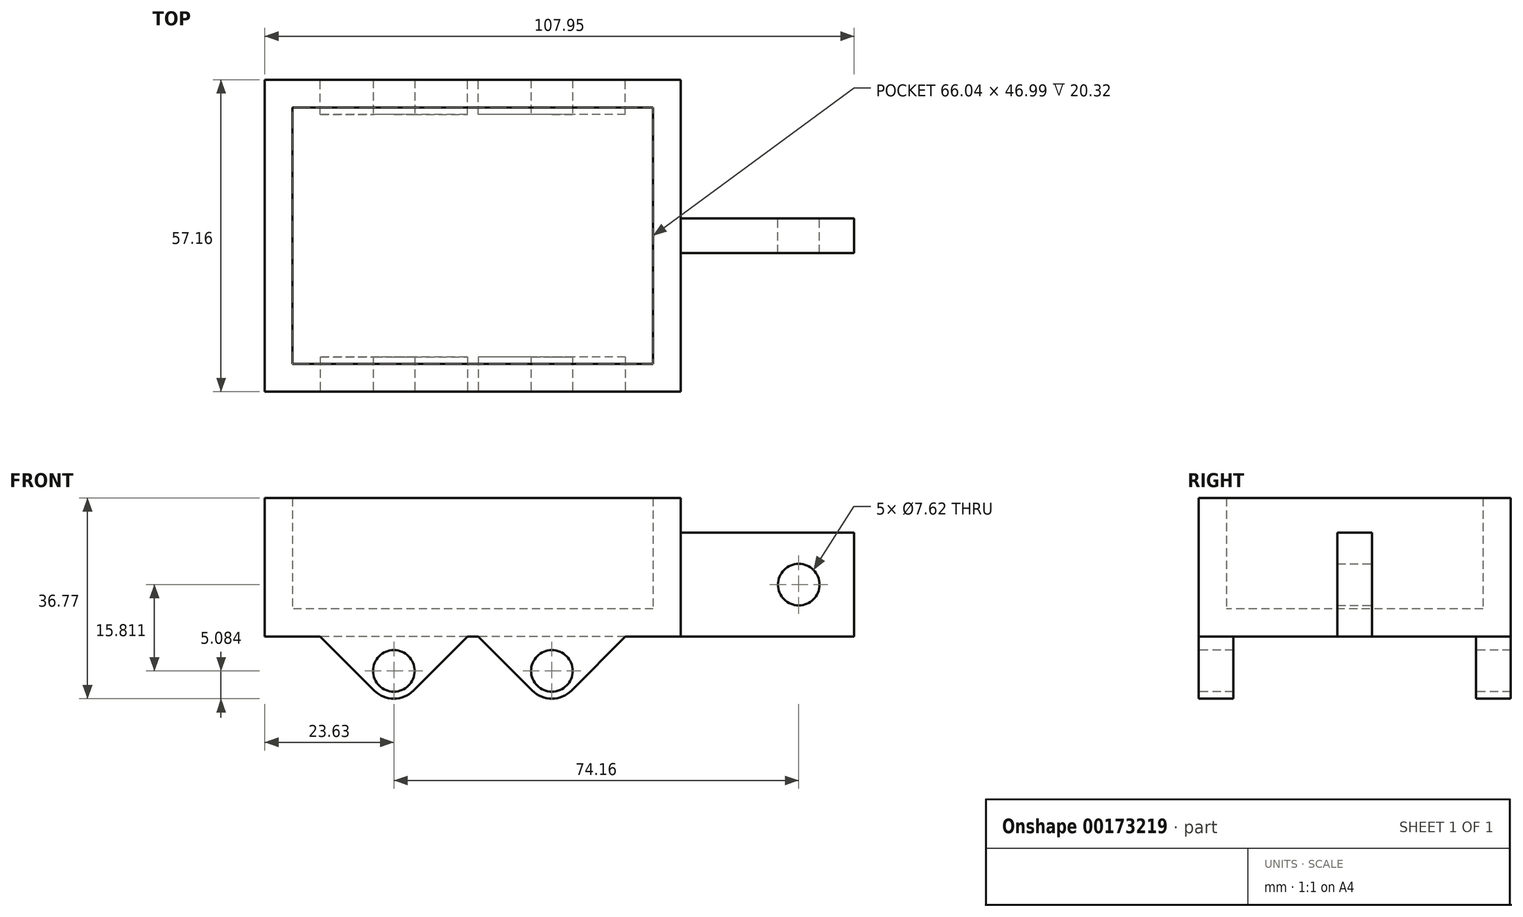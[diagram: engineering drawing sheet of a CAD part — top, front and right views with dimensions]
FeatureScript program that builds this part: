
annotation { "Feature Type Name" : "Feature", "Feature Type Description" : "" }
export const myFeature = defineFeature(function(context is Context, id is Id, definition is map)
    precondition{}
    {
        {
            var Q0;
            Q0=qCreatedBy(makeId("Top.planeOp"),FACE);
            var sketch = newSketch(context, id + "F0", { "sketchPlane" : qUnion([Q0])});
            skLineSegment(sketch, "E0.bottom", {"start": v(38.1, 28.58) * mm, "end": v(-38.1, 28.58) * mm});
            skLineSegment(sketch, "E0.top", {"start": v(38.1, -28.58) * mm, "end": v(-38.1, -28.58) * mm});
            skLineSegment(sketch, "E0.left", {"start": v(38.1, 28.58) * mm, "end": v(38.1, -28.58) * mm});
            skLineSegment(sketch, "E0.right", {"start": v(-38.1, 28.58) * mm, "end": v(-38.1, -28.58) * mm});
            skPoint(sketch, "E0.middle", {"position": v(0, 0) * mm});
            skSolve(sketch);
        }
        {
            var Q0;
            Q0=makeQuery(id+"F0.imprint","IMPRINT",FACE,{"disambiguationData":[TD([[makeQuery(id+"F0.imprint","IMPRINT",EDGE,{"derivedFrom":sQuery(id+"F0.wireOp",EDGE,"E0.bottom")}),1.0]])]});
            extrude(context, id + "F1", {"entities" : qUnion([Q0]), "depth" : 25.4 * mm});
        }
        {
            var Q0;
            Q0=makeQuery(id+"F1.opExtrude","CAP_FACE",FACE,{"disambiguationData":[OSD([sQuery(id+"F0.wireOp",EDGE,"E0.bottom"),sQuery(id+"F0.wireOp",EDGE,"E0.top"),sQuery(id+"F0.wireOp",EDGE,"E0.left"),sQuery(id+"F0.wireOp",EDGE,"E0.right")])],"isStart":false});
            shell(context, id + "F2", {"entities" : qUnion([Q0]), "thickness" : 5.08 * mm});
        }
        {
            var Q0;
            Q0=makeQuery(id+"F1.opExtrude","SWEPT_FACE",FACE,{"disambiguationData":[OSD([sQuery(id+"F0.wireOp",EDGE,"E0.top")])]});
            var sketch = newSketch(context, id + "F3", { "sketchPlane" : qUnion([Q0])});
            skLineSegment(sketch, "E1", {"start": v(-27.94, 0) * mm, "end": v(-38.1, 0) * mm});
            skLineSegment(sketch, "E2", {"start": v(-27.94, 0) * mm, "end": v(-14.47, -13.47) * mm});
            skLineSegment(sketch, "E3", {"start": v(-14.47, -13.47) * mm, "end": v(-1, 0) * mm});
            skLineSegment(sketch, "E4", {"start": v(38.1, 0) * mm, "end": v(27.94, 0) * mm});
            skLineSegment(sketch, "E5", {"start": v(27.94, 0) * mm, "end": v(14.47, -13.47) * mm});
            skLineSegment(sketch, "E6", {"start": v(14.47, -13.47) * mm, "end": v(1, 0) * mm});
            skSolve(sketch);
        }
        {
            var Q0;
            {var subQ0=sQuery(id+"F3.wireOp",EDGE,"E2");Q0=makeQuery(id+"F3.imprint","IMPRINT",FACE,{"disambiguationData":[TD([[makeQuery(id+"F3.imprint","IMPRINT",EDGE,{"derivedFrom":subQ0}),1.0]])]});}
            var Q1;
            {var subQ0=sQuery(id+"F3.wireOp",EDGE,"E5");Q1=makeQuery(id+"F3.imprint","IMPRINT",FACE,{"disambiguationData":[TD([[makeQuery(id+"F3.imprint","IMPRINT",EDGE,{"derivedFrom":subQ0}),-1.0]])]});}
            extrude(context, id + "F4", {"entities" : qUnion([Q0, Q1]), "operationType" : NewBodyOperationType.ADD, "oppositeDirection" : true, "depth" : 6.35 * mm});
        }
        {
            var Q0;
            Q0=makeQuery(id+"F4.opExtrude","SWEPT_EDGE",EDGE,{"disambiguationData":[OSD([sQuery(id+"F3.wireOp",EDGE,"E2"),sQuery(id+"F3.wireOp",EDGE,"E3")])]});
            var Q1;
            Q1=makeQuery(id+"F4.opExtrude","SWEPT_EDGE",EDGE,{"disambiguationData":[OSD([sQuery(id+"F3.wireOp",EDGE,"E5"),sQuery(id+"F3.wireOp",EDGE,"E6")])]});
            fillet(context, id + "F5", {"entities" : qUnion([Q0, Q1]), "radius" : 5.08 * mm, "tangentPropagation" : true, "allowEdgeOverflow" : false});
        }
        {
            var Q0;
            {var subQ0=sQuery(id+"F0.wireOp",EDGE,"E0.top");Q0=makeQuery(id+"F4.boolean.opBoolean","MERGE",FACE,{"derivedFrom":[makeQuery(id+"F1.opExtrude","SWEPT_FACE",FACE,{"disambiguationData":[OSD([subQ0])]}),makeQuery(id+"F4.opExtrude","CAP_FACE",FACE,{"disambiguationData":[OSD([subQ0,sQuery(id+"F3.wireOp",EDGE,"E2"),sQuery(id+"F3.wireOp",EDGE,"E3")])],"isStart":true}),makeQuery(id+"F4.opExtrude","CAP_FACE",FACE,{"disambiguationData":[OSD([subQ0,sQuery(id+"F3.wireOp",EDGE,"E5"),sQuery(id+"F3.wireOp",EDGE,"E6")])],"isStart":true})]});}
            var sketch = newSketch(context, id + "F6", { "sketchPlane" : qUnion([Q0])});
            skCircle(sketch, "E7", {"center": v(-14.47, -6.29) * mm, "radius": 3.81 * mm});
            skCircle(sketch, "E8", {"center": v(14.47, -6.29) * mm, "radius": 3.81 * mm});
            skSolve(sketch);
        }
        {
            var Q0;
            Q0=makeQuery(id+"F1.opExtrude","SWEPT_FACE",FACE,{"disambiguationData":[OSD([sQuery(id+"F0.wireOp",EDGE,"E0.bottom")])]});
            var sketch = newSketch(context, id + "F7", { "sketchPlane" : qUnion([Q0])});
            skLineSegment(sketch, "E9", {"start": v(-38.1, 0) * mm, "end": v(-27.94, 0) * mm});
            skLineSegment(sketch, "E10", {"start": v(-27.94, 0) * mm, "end": v(-14.47, -13.47) * mm});
            skLineSegment(sketch, "E11", {"start": v(-14.47, -13.47) * mm, "end": v(-1, 0) * mm});
            skLineSegment(sketch, "E12", {"start": v(38.1, 0) * mm, "end": v(27.94, 0) * mm});
            skLineSegment(sketch, "E13", {"start": v(27.94, 0) * mm, "end": v(14.47, -13.47) * mm});
            skLineSegment(sketch, "E14", {"start": v(14.47, -13.47) * mm, "end": v(1, 0) * mm});
            skSolve(sketch);
        }
        {
            var Q0;
            {var subQ0=sQuery(id+"F7.wireOp",EDGE,"E10");Q0=makeQuery(id+"F7.imprint","IMPRINT",FACE,{"disambiguationData":[TD([[makeQuery(id+"F7.imprint","IMPRINT",EDGE,{"derivedFrom":subQ0}),1.0]])]});}
            var Q1;
            {var subQ0=sQuery(id+"F7.wireOp",EDGE,"E13");Q1=makeQuery(id+"F7.imprint","IMPRINT",FACE,{"disambiguationData":[TD([[makeQuery(id+"F7.imprint","IMPRINT",EDGE,{"derivedFrom":subQ0}),-1.0]])]});}
            extrude(context, id + "F8", {"entities" : qUnion([Q0, Q1]), "operationType" : NewBodyOperationType.ADD, "oppositeDirection" : true, "depth" : 6.35 * mm});
        }
        {
            var Q0;
            Q0=sQuery(id+"F6.wireOp",VERTEX,"E7.center");
            var Q1;
            Q1=sQuery(id+"F6.wireOp",VERTEX,"E8.center");
            var Q2;
            Q2=makeQuery(id+"F1.opExtrude","SWEPT_BODY",BODY,{"disambiguationData":[OSD([sQuery(id+"F0.wireOp",EDGE,"E0.bottom"),sQuery(id+"F0.wireOp",EDGE,"E0.top"),sQuery(id+"F0.wireOp",EDGE,"E0.left"),sQuery(id+"F0.wireOp",EDGE,"E0.right")])]});
            hole(context, id + "F9", {"style" : HoleStyle.SIMPLE, "endStyle" : HoleEndStyle.THROUGH, "holeDiameter" : 7.62 * mm, "locations" : qUnion([Q0, Q1]), "scope" : qUnion([Q2]), "isTappedThrough" : true});
        }
        {
            var Q0;
            Q0=makeQuery(id+"F8.opExtrude","SWEPT_EDGE",EDGE,{"disambiguationData":[OSD([sQuery(id+"F7.wireOp",EDGE,"E10"),sQuery(id+"F7.wireOp",EDGE,"E11")])]});
            var Q1;
            Q1=makeQuery(id+"F8.opExtrude","SWEPT_EDGE",EDGE,{"disambiguationData":[OSD([sQuery(id+"F7.wireOp",EDGE,"E13"),sQuery(id+"F7.wireOp",EDGE,"E14")])]});
            fillet(context, id + "F10", {"entities" : qUnion([Q0, Q1]), "radius" : 5.08 * mm, "tangentPropagation" : true, "allowEdgeOverflow" : false});
        }
        {
            var Q0;
            Q0=makeQuery(id+"F1.opExtrude","SWEPT_FACE",FACE,{"disambiguationData":[OSD([sQuery(id+"F0.wireOp",EDGE,"E0.left")])]});
            var sketch = newSketch(context, id + "F11", { "sketchPlane" : qUnion([Q0])});
            skLineSegment(sketch, "E15", {"start": v(-28.57, 0) * mm, "end": v(-3.17, 0) * mm});
            skLineSegment(sketch, "E16", {"start": v(28.58, 0) * mm, "end": v(3.18, 0) * mm});
            skLineSegment(sketch, "E17.bottom", {"start": v(-3.17, 0) * mm, "end": v(3.18, 0) * mm});
            skLineSegment(sketch, "E17.top", {"start": v(-3.17, 19.05) * mm, "end": v(3.18, 19.05) * mm});
            skLineSegment(sketch, "E17.left", {"start": v(-3.17, 0) * mm, "end": v(-3.17, 19.05) * mm});
            skLineSegment(sketch, "E17.right", {"start": v(3.18, 0) * mm, "end": v(3.18, 19.05) * mm});
            skLineSegment(sketch, "E18", {"start": v(3.18, 0) * mm, "end": v(28.58, 0) * mm});
            skLineSegment(sketch, "E19", {"start": v(-3.17, 0) * mm, "end": v(-28.57, 0) * mm});
            skSolve(sketch);
        }
        {
            var Q0;
            Q0=makeQuery(id+"F11.imprint","IMPRINT",FACE,{"disambiguationData":[TD([[makeQuery(id+"F11.imprint","IMPRINT",EDGE,{"derivedFrom":sQuery(id+"F11.wireOp",EDGE,"E17.bottom")}),-1.0]])]});
            extrude(context, id + "F12", {"entities" : qUnion([Q0]), "operationType" : NewBodyOperationType.ADD, "depth" : 31.75 * mm});
        }
        {
            var Q0;
            Q0=makeQuery(id+"F12.opExtrude","SWEPT_FACE",FACE,{"disambiguationData":[OSD([sQuery(id+"F11.wireOp",EDGE,"E17.right")])]});
            var sketch = newSketch(context, id + "F13", { "sketchPlane" : qUnion([Q0])});
            skPoint(sketch, "E20.oppositeSnap0", {"position": v(-69.85, 9.53) * mm});
            skPoint(sketch, "E20.oppositeSnap1", {"position": v(-59.69, 19.05) * mm});
            skCircle(sketch, "E21", {"center": v(-59.69, 9.53) * mm, "radius": 3.81 * mm});
            skLineSegment(sketch, "E22", {"start": v(-59.69, 9.52) * mm, "end": v(-69.85, 9.52) * mm});
            skSolve(sketch);
        }
        {
            var Q0;
            Q0=sQuery(id+"F13.wireOp",VERTEX,"E21.center");
            var Q1;
            Q1=makeQuery(id+"F1.opExtrude","SWEPT_BODY",BODY,{"disambiguationData":[OSD([sQuery(id+"F0.wireOp",EDGE,"E0.bottom"),sQuery(id+"F0.wireOp",EDGE,"E0.top"),sQuery(id+"F0.wireOp",EDGE,"E0.left"),sQuery(id+"F0.wireOp",EDGE,"E0.right")])]});
            hole(context, id + "F14", {"style" : HoleStyle.SIMPLE, "endStyle" : HoleEndStyle.THROUGH, "holeDiameter" : 7.62 * mm, "locations" : qUnion([Q0]), "scope" : qUnion([Q1]), "isTappedThrough" : true});
        }
    });
